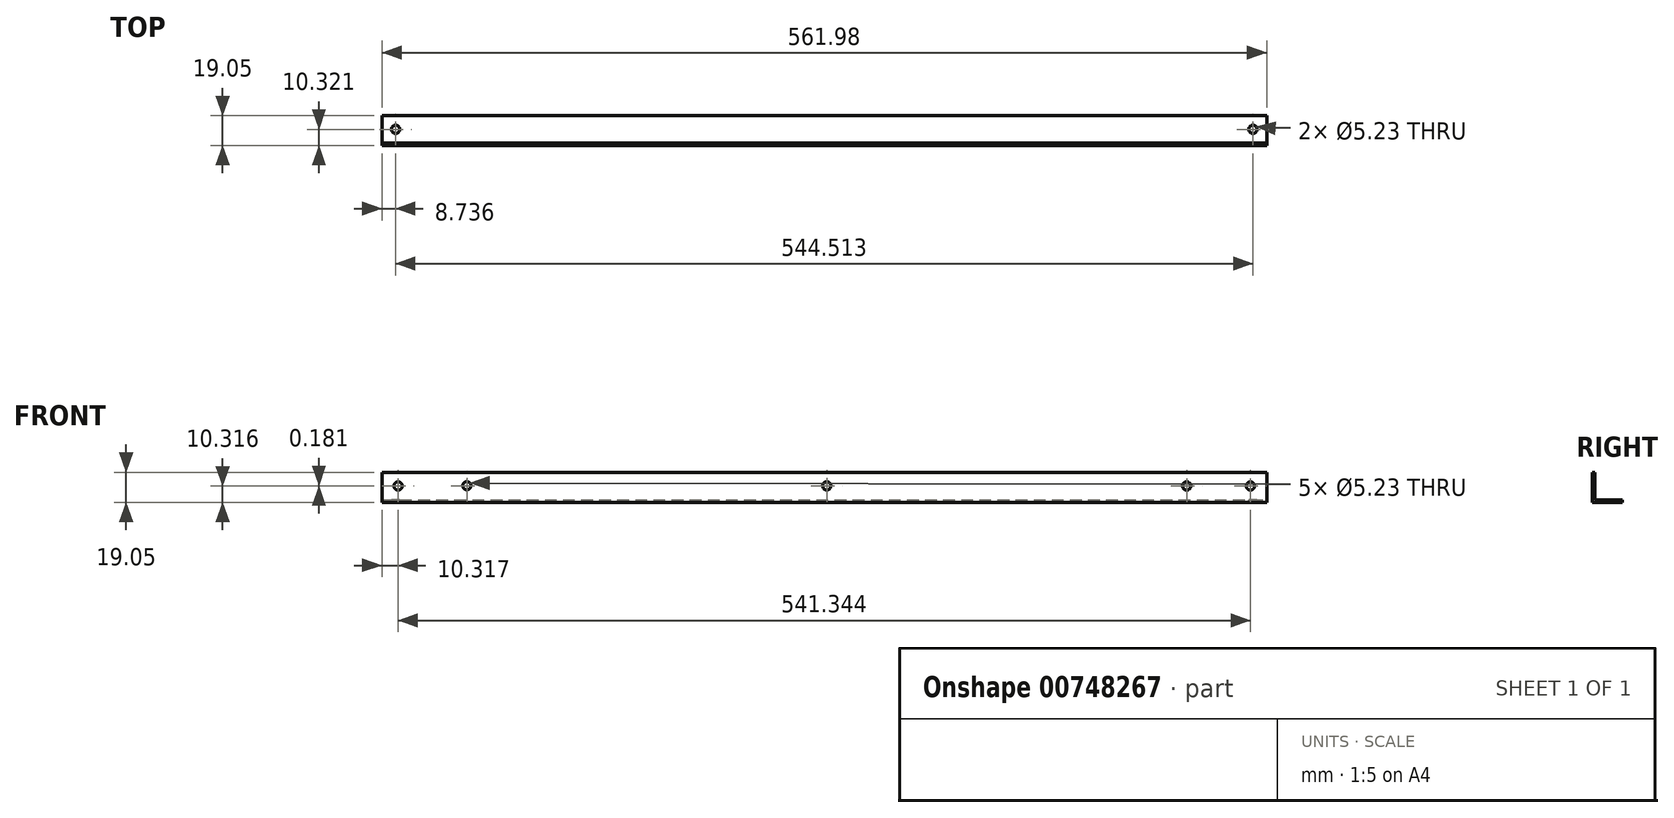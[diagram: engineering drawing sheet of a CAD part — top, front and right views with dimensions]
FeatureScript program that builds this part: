
annotation { "Feature Type Name" : "Feature", "Feature Type Description" : "" }
export const myFeature = defineFeature(function(context is Context, id is Id, definition is map)
    precondition{}
    {
        {
            var Q0;
            Q0=qCreatedBy(makeId("Right.planeOp"),FACE);
            var sketch = newSketch(context, id + "F0", { "sketchPlane" : qUnion([Q0])});
            skLineSegment(sketch, "E0", {"start": v(0, 0) * mm, "end": v(0, -17.46) * mm});
            skLineSegment(sketch, "E1", {"start": v(0, -17.46) * mm, "end": v(17.46, -17.46) * mm});
            skLineSegment(sketch, "E2.0", {"start": v(-1.59, -19.05) * mm, "end": v(17.46, -19.05) * mm});
            skLineSegment(sketch, "E2.1", {"start": v(-1.59, 0) * mm, "end": v(-1.59, -19.05) * mm});
            skLineSegment(sketch, "E3", {"start": v(-1.59, 0) * mm, "end": v(0, 0) * mm});
            skLineSegment(sketch, "E4", {"start": v(17.46, -17.46) * mm, "end": v(17.46, -19.05) * mm});
            skSolve(sketch);
        }
        {
            var Q0;
            Q0=makeQuery(id+"F0.imprint","IMPRINT",FACE,{"disambiguationData":[TD([[makeQuery(id+"F0.imprint","IMPRINT",EDGE,{"derivedFrom":sQuery(id+"F0.wireOp",EDGE,"E0")}),-1.0]])]});
            extrude(context, id + "F1", {"entities" : qUnion([Q0]), "oppositeDirection" : true, "depth" : 561.98 * mm, "offsetDistance" : 25.4 * mm});
        }
        {
            var Q0;
            Q0=makeQuery(id+"F1.opExtrude","SWEPT_FACE",FACE,{"disambiguationData":[OSD([sQuery(id+"F0.wireOp",EDGE,"E0")])]});
            var sketch = newSketch(context, id + "F2", { "sketchPlane" : qUnion([Q0])});
            skLineSegment(sketch, "E5", {"start": v(0, -8.74) * mm, "end": v(558.8, -8.53) * mm, "construction": true});
            skLineSegment(sketch, "E6.top", {"start": v(0, -17.46) * mm, "end": v(10.32, -17.46) * mm, "construction": true});
            skLineSegment(sketch, "E6.right", {"start": v(10.32, 0) * mm, "end": v(10.32, -17.46) * mm, "construction": true});
            skLineSegment(sketch, "E7.right", {"start": v(551.66, 0) * mm, "end": v(551.66, -17.46) * mm, "construction": true});
            skCircle(sketch, "E8", {"center": v(10.32, -8.73) * mm, "radius": 2.62 * mm});
            skCircle(sketch, "E9", {"center": v(279.4, -8.64) * mm, "radius": 2.62 * mm});
            skCircle(sketch, "E10", {"center": v(551.66, -8.73) * mm, "radius": 2.62 * mm});
            skLineSegment(sketch, "E11", {"start": v(279.4, 0) * mm, "end": v(279.4, -17.46) * mm, "construction": true});
            skLineSegment(sketch, "E12", {"start": v(203.2, 0) * mm, "end": v(203.2, -17.46) * mm, "construction": true});
            skLineSegment(sketch, "E13", {"start": v(355.6, 0) * mm, "end": v(355.6, -17.46) * mm, "construction": true});
            skLineSegment(sketch, "E14", {"start": v(127, 0) * mm, "end": v(127, -17.46) * mm, "construction": true});
            skLineSegment(sketch, "E15", {"start": v(431.8, 0) * mm, "end": v(431.8, -17.46) * mm, "construction": true});
            skLineSegment(sketch, "E16", {"start": v(50.8, 0) * mm, "end": v(50.8, -17.46) * mm, "construction": true});
            skLineSegment(sketch, "E17", {"start": v(508, 0) * mm, "end": v(508, -17.46) * mm, "construction": true});
            skCircle(sketch, "E18", {"center": v(508, -8.55) * mm, "radius": 2.62 * mm});
            skCircle(sketch, "E19", {"center": v(50.8, -8.72) * mm, "radius": 2.62 * mm});
            skPoint(sketch, "E19.centerSnap0", {"position": v(50.8, -8.73) * mm});
            skSolve(sketch);
        }
        {
            var Q0;
            Q0=makeQuery(id+"F1.opExtrude","SWEPT_FACE",FACE,{"disambiguationData":[OSD([sQuery(id+"F0.wireOp",EDGE,"E1")])]});
            var sketch = newSketch(context, id + "F3", { "sketchPlane" : qUnion([Q0])});
            skLineSegment(sketch, "E20", {"start": v(0, 8.73) * mm, "end": v(-561.98, 8.73) * mm, "construction": true});
            skLineSegment(sketch, "E21.bottom", {"start": v(0, 0) * mm, "end": v(-8.73, 0) * mm, "construction": true});
            skLineSegment(sketch, "E21.top", {"start": v(0, 17.46) * mm, "end": v(-8.73, 17.46) * mm, "construction": true});
            skLineSegment(sketch, "E21.left", {"start": v(0, 0) * mm, "end": v(0, 17.46) * mm, "construction": true});
            skLineSegment(sketch, "E21.right", {"start": v(-8.73, 0) * mm, "end": v(-8.73, 17.46) * mm, "construction": true});
            skLineSegment(sketch, "E22.bottom", {"start": v(-561.98, 0) * mm, "end": v(-553.24, 0) * mm, "construction": true});
            skLineSegment(sketch, "E22.top", {"start": v(-561.98, 17.46) * mm, "end": v(-553.24, 17.46) * mm, "construction": true});
            skLineSegment(sketch, "E22.left", {"start": v(-561.98, 0) * mm, "end": v(-561.98, 17.46) * mm, "construction": true});
            skLineSegment(sketch, "E22.right", {"start": v(-553.24, 0) * mm, "end": v(-553.24, 17.46) * mm, "construction": true});
            skCircle(sketch, "E23", {"center": v(-8.73, 8.73) * mm, "radius": 2.62 * mm});
            skCircle(sketch, "E24", {"center": v(-553.24, 8.73) * mm, "radius": 2.62 * mm});
            skSolve(sketch);
        }
        {
            var Q0;
            Q0 = qSketchRegion(id + "F2", true);
            extrude(context, id + "F4", {"entities" : qUnion([Q0]), "operationType" : NewBodyOperationType.REMOVE, "oppositeDirection" : true, "depth" : 25.4 * mm, "offsetDistance" : 25.4 * mm});
        }
        {
            var Q0;
            Q0 = qSketchRegion(id + "F3", true);
            extrude(context, id + "F5", {"entities" : qUnion([Q0]), "operationType" : NewBodyOperationType.REMOVE, "oppositeDirection" : true, "depth" : 25.4 * mm, "offsetDistance" : 25.4 * mm});
        }
    });
